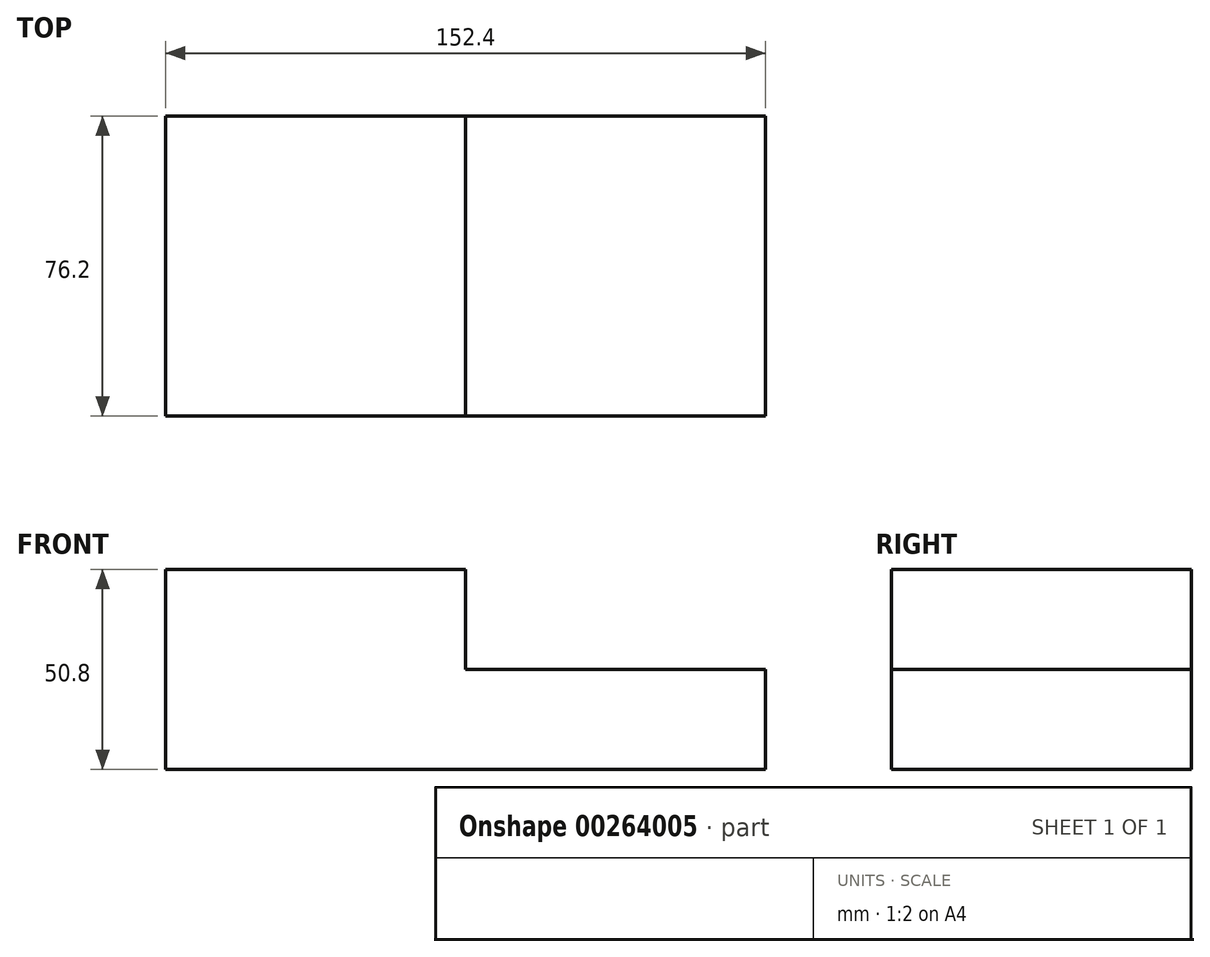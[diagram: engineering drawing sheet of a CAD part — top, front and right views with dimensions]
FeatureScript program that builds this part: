
annotation { "Feature Type Name" : "Feature", "Feature Type Description" : "" }
export const myFeature = defineFeature(function(context is Context, id is Id, definition is map)
    precondition{}
    {
        {
            var Q0;
            Q0=qCreatedBy(makeId("Front.planeOp"),FACE);
            var sketch = newSketch(context, id + "F0", { "sketchPlane" : qUnion([Q0])});
            skLineSegment(sketch, "E0", {"start": v(0, 0) * mm, "end": v(-76.2, 0) * mm});
            skLineSegment(sketch, "E1", {"start": v(-76.2, 0) * mm, "end": v(-76.2, 50.8) * mm});
            skLineSegment(sketch, "E2", {"start": v(-76.2, 50.8) * mm, "end": v(0, 50.8) * mm});
            skLineSegment(sketch, "E3", {"start": v(0, 50.8) * mm, "end": v(0, 25.4) * mm});
            skLineSegment(sketch, "E4", {"start": v(0, 0) * mm, "end": v(76.2, 0) * mm});
            skLineSegment(sketch, "E5", {"start": v(76.2, 0) * mm, "end": v(76.2, 25.4) * mm});
            skLineSegment(sketch, "E6", {"start": v(76.2, 25.4) * mm, "end": v(0, 25.4) * mm});
            skSolve(sketch);
        }
        {
            var Q0;
            Q0=makeQuery(id+"F0.imprint","IMPRINT",FACE,{"disambiguationData":[TD([[makeQuery(id+"F0.imprint","IMPRINT",EDGE,{"derivedFrom":sQuery(id+"F0.wireOp",EDGE,"E0")}),-1.0]])]});
            extrude(context, id + "F1", {"entities" : qUnion([Q0]), "depth" : 38.1 * mm});
        }
        {
            var Q0;
            Q0=makeQuery(id+"F1.opExtrude","CAP_FACE",FACE,{"disambiguationData":[OSD([sQuery(id+"F0.wireOp",EDGE,"E0"),sQuery(id+"F0.wireOp",EDGE,"E1"),sQuery(id+"F0.wireOp",EDGE,"E2"),sQuery(id+"F0.wireOp",EDGE,"E3"),sQuery(id+"F0.wireOp",EDGE,"E4"),sQuery(id+"F0.wireOp",EDGE,"E5"),sQuery(id+"F0.wireOp",EDGE,"E6")])],"isStart":true});
            extrude(context, id + "F2", {"entities" : qUnion([Q0]), "operationType" : NewBodyOperationType.ADD, "depth" : 38.1 * mm});
        }
    });
